# Revit family: Legrand_Digital_Management_Building_LIGHTUP_Sensor
name_source: partatom
category: Dispositifs d'éclairage
units: mm (PartAtom-declared; Revit-internal decimal feet)

## family parameters
Conserver l'orientation des annotations = Non
Cote de connecteur circulaire = Utiliser le diamètre
Couper avec des vides une fois chargée = Non
Hôte = Face
Numéro OmniClass = 23.85.80.11.27
Partagée = Non
Repere pour localisation dans la piece = Non
Titre OmniClass = Lighting Controls
Type d'élément = Normal

## types (10) — shared parameters
Bluetooth BLE = Oui
Color = White
Configurable Zones = Oui
Configurable distance = Oui
Detection angle horizontal = 360°
ETIM Class = EC001582-Movement sensor for bus system
Elévation par défaut = 2500 mm  [stored 8.2021 ft]
Fabricant = LEGRAND
Frequency = 50/60 Hz
General Conditions of Use = https://export.legrand.com
Hauteur_Saillie = 93 mm  [stored 0.305118 ft]
IK = 04
IP = 20
Installation method = Flush or surface mounting
Material = LEGRAND_PVC_BLANC
Model Product = Movement sensor
Optimum mounting height = 2500 mm  [stored 8.2021 ft]
Power supply = 240 VAC
Remote operation = Oui
Response value luminosity = 5 LUX -1275 LUX
Response value luminosity adjustable = Oui
Suitable for wireless transmission = Oui
URL = https://www.legrand.fr
With remote control = Oui
Zigbee = Oui

## per-type parameters (varying)
- CORRIDOR OCCUPANCY DETECTOR DALI: Communication Protocol=Radio 2,4 GHz;Bluetooth 5.0;DALI-2; Dali=Oui; Description=Light Up connectable presence detector for DALI broadcast circuit with variation, special for passageways; Diameter=0 mm  [stored 0 ft]; Diameter detection range on floor=0 mm  [stored 0 ft]; EAN Code=3414972281195; Etiquette_ZD_BASIC_MULTI=Non; Etiquette_ZD_CORRIDOR=Oui; Etiquette_ZD_ZS_ACTIVITY_ADVANCED=Non; Famille imbriquée=CORRIDOR_SENSOR; Height=96 mm  [stored 0.314961 ft]; Length=103 mm; Max. transmission range frontally=24000 mm  [stored 78.7402 ft]; Max. transmission range sideways=3000 mm  [stored 9.84252 ft]; Mounting height (Min-Max)=1700 mm-4000 mm; Operating temperature MIN-MAX=-10°C - +30 °C; Product designation=LIGHT UP CORRIDOR DALI DETECTOR; Reference=048554; Response value sensitivity adjustable=Oui; Sensor type=infrared; Shape detection=round; Surface detection=72 m2; Weight=213.75 g; Width=103 mm; Zones=ZD_CORRIDOR
- OCCUPANCY DETECTOR DALI: Communication Protocol=Radio 2,4 GHz;Bluetooth 5.0;DALI-2; Dali=Oui; Description=Light Up connectable presence detector for DALI broadcast circuit with variation, special workspace; Diameter=83 mm  [stored 0.27231 ft]; Diameter detection range on floor=12000 mm; EAN Code=3414972281171; Etiquette_ZD_BASIC_MULTI=Oui; Etiquette_ZD_CORRIDOR=Non; Etiquette_ZD_ZS_ACTIVITY_ADVANCED=Non; Famille imbriquée=BASIC_SENSOR; Height=83 mm  [stored 0.27231 ft]; Length=83 mm  [stored 0.27231 ft]; Max. transmission range frontally=0 mm  [stored 0 ft]; Max. transmission range sideways=0 mm  [stored 0 ft]; Mounting height (Min-Max)=1700 mm-4000 mm; Operating temperature MIN-MAX=-10°C - +30 °C; Product designation=LIGHT UP OCCUPANCY DALI DETECTOR; Reference=048552; Response value sensitivity adjustable=Oui; Sensor type=infrared; Shape detection=round; Surface detection=112 m2; Weight=142.5 g; Width=83 mm  [stored 0.27231 ft]; Zones=ZD_BASIC_MULTI
- OCCUPANCY DETECTOR ON-OFF: Communication Protocol=Radio 2,4 GHz;Bluetooth 5.0; Dali=Non; Description=Light Up ON/OFF connectable presence detector, special workspace; Diameter=83 mm  [stored 0.27231 ft]; Diameter detection range on floor=12000 mm; EAN Code=3414972281188; Etiquette_ZD_BASIC_MULTI=Oui; Etiquette_ZD_CORRIDOR=Non; Etiquette_ZD_ZS_ACTIVITY_ADVANCED=Non; Famille imbriquée=BASIC_SENSOR; Height=83 mm  [stored 0.27231 ft]; Length=83 mm  [stored 0.27231 ft]; Max. switching power=2000 W; Max. transmission range frontally=0 mm  [stored 0 ft]; Max. transmission range sideways=0 mm  [stored 0 ft]; Mounting height (Min-Max)=1700 mm-4000 mm; Operating temperature MIN-MAX=-10°C - +30 °C; Product designation=LIGHT UP OCCUPANCY ON-OFF DETECTOR; Reference=048551; Response value sensitivity adjustable=Oui; Sensor type=infrared; Shape detection=round; Surface detection=112 m2; Weight=161.5 g; Width=83 mm  [stored 0.27231 ft]; Zones=ZD_BASIC_MULTI
- OCCUPANCY DETECTOR DALI 3 ZONES: Communication Protocol=Radio 2,4 GHz;Bluetooth 5.0;DALI-2; Dali=Oui; Description=Light Up connectable presence detector for multicast DALI circuit with variation, special workspace; Diameter=83 mm  [stored 0.27231 ft]; Diameter detection range on floor=12000 mm; EAN Code=3414972406239; Etiquette_ZD_BASIC_MULTI=Oui; Etiquette_ZD_CORRIDOR=Non; Etiquette_ZD_ZS_ACTIVITY_ADVANCED=Non; Famille imbriquée=BASIC_SENSOR; Height=83 mm  [stored 0.27231 ft]; Length=83 mm  [stored 0.27231 ft]; Max. transmission range frontally=0 mm  [stored 0 ft]; Max. transmission range sideways=0 mm  [stored 0 ft]; Mounting height (Min-Max)=1700 mm-4000 mm; Operating temperature MIN-MAX=-10°C - +30 °C; Product designation=LIGHT UP OCCUPANCY DALI 3 ZONES DETECTOR; Reference=048555; Response value sensitivity adjustable=Oui; Sensor type=infrared; Shape detection=round; Surface detection=112 m2; Weight=161.5 g; Width=83 mm  [stored 0.27231 ft]; Zones=ZD_BASIC_MULTI
- CORRIDOR OCCUPANCY DETECTOR ON-OFF: Communication Protocol=Radio 2,4 GHz;Bluetooth 5.0; Dali=Non; Description=Connectable presence detector Light Up ON/OFF, special for places of passage; Diameter=103 mm; Diameter detection range on floor=0 mm  [stored 0 ft]; EAN Code=3414972281164; Etiquette_ZD_BASIC_MULTI=Non; Etiquette_ZD_CORRIDOR=Oui; Etiquette_ZD_ZS_ACTIVITY_ADVANCED=Non; Famille imbriquée=CORRIDOR_SENSOR; Height=96 mm  [stored 0.314961 ft]; Length=103 mm; Max. switching power=2000 W; Max. transmission range frontally=24000 mm  [stored 78.7402 ft]; Max. transmission range sideways=3000 mm  [stored 9.84252 ft]; Mounting height (Min-Max)=1700 mm-4000 mm; Operating temperature MIN-MAX=-10°C - +30 °C; Product designation=LIGHT UP CORRIDOR ON-OFF DETECTOR; Reference=048553; Response value sensitivity adjustable=Oui; Sensor type=infrared; Shape detection=round; Surface detection=72 m2; Weight=242.25 g; Width=103 mm; Zones=ZD_CORRIDOR
- MULTISENSOR DALI 3 ZONES DETECTOR: Communication Protocol=Radio 2,4 GHz;Bluetooth 5.0;DALI-2; Dali=Oui; Description=Light Up connectable presence detector for multicast DALI circuit with variation and environmental measurements; Diameter=103 mm; Diameter detection range on floor=12000 mm; EAN Code=3414972406253; Etiquette_ZD_BASIC_MULTI=Oui; Etiquette_ZD_CORRIDOR=Non; Etiquette_ZD_ZS_ACTIVITY_ADVANCED=Non; Famille imbriquée=MULTI_SENSOR; Height=85 mm; Length=103 mm; Max. switching power=1500 W; Max. transmission range frontally=0 mm  [stored 0 ft]; Max. transmission range sideways=0 mm  [stored 0 ft]; Mounting height (Min-Max)=1700 mm-4000 mm; Operating temperature MIN-MAX=-10°C - +30 °C; Product designation=LIGHT UP MULTISENSOR DALI 3 ZONES DETECTORv; Reference=048573; Response value sensitivity adjustable=Oui; Sensor type=infrared; Shape detection=round; Surface detection=112 m2; Weight=223.25 g; Width=103 mm; Zones=ZD_BASIC_MULTI
- MULTISENSOR DALI DETECTOR: Communication Protocol=Radio 2,4 GHz;Bluetooth 5.0;DALI-2; Dali=Oui; Description=Light Up connectable presence detector for DALI broadcast circuit with variation and environmental measurements; Diameter=103 mm; Diameter detection range on floor=12000 mm; EAN Code=3414972281157; Etiquette_ZD_BASIC_MULTI=Oui; Etiquette_ZD_CORRIDOR=Non; Etiquette_ZD_ZS_ACTIVITY_ADVANCED=Non; Famille imbriquée=MULTI_SENSOR; Height=85 mm; Length=103 mm; Max. switching power=1500 W; Max. transmission range frontally=0 mm  [stored 0 ft]; Max. transmission range sideways=0 mm  [stored 0 ft]; Mounting height (Min-Max)=1700 mm-4000 mm; Operating temperature MIN-MAX=-10°C - +30 °C; Product designation=LIGHT UP MULTISENSOR DALI DETECTOR; Reference=048571; Response value sensitivity adjustable=Oui; Sensor type=infrared; Shape detection=round; Surface detection=112 m2; Weight=223.25 g; Width=103 mm; Zones=ZD_BASIC_MULTI
- CORRIDOR OCCUPANCY DETECTOR DALI 3 ZONES: Communication Protocol=Radio 2,4 GHz;Bluetooth 5.0;DALI-2; Dali=Oui; Description=Light Up connectable presence detector for DALI multicast circuit with variation, special for passageways; Diameter=0 mm  [stored 0 ft]; Diameter detection range on floor=0 mm  [stored 0 ft]; EAN Code=3414972406246; Etiquette_ZD_BASIC_MULTI=Non; Etiquette_ZD_CORRIDOR=Oui; Etiquette_ZD_ZS_ACTIVITY_ADVANCED=Non; Famille imbriquée=CORRIDOR_SENSOR; Height=96 mm  [stored 0.314961 ft]; Length=103 mm; Max. transmission range frontally=24000 mm  [stored 78.7402 ft]; Max. transmission range sideways=3000 mm  [stored 9.84252 ft]; Mounting height (Min-Max)=1700 mm-4000 mm; Operating temperature MIN-MAX=-10°C - +30 °C; Product designation=LIGHT UP CORRIDOR DALI 3 ZONES DETECTOR; Reference=048556; Response value sensitivity adjustable=Oui; Sensor type=infrared; Shape detection=round; Surface detection=72 m2; Weight=242.25 g; Width=103 mm; Zones=ZD_CORRIDOR
- ADVANCED MULTISENSOR DALI 3 ZONES DETECTOR: Communication Protocol=Radio 2,4 GHz;Bluetooth 5.0;DALI-2; Dali=Oui; Description=Light Up connectable presence detector for multicast DALI circuit with variation, environmental measurements, people counting; Diameter=0 mm  [stored 0 ft]; Diameter detection range on floor=0 mm  [stored 0 ft]; EAN Code=3414972406260; Etiquette_ZD_BASIC_MULTI=Non; Etiquette_ZD_CORRIDOR=Non; Etiquette_ZD_ZS_ACTIVITY_ADVANCED=Oui; Famille imbriquée=ADVANCED_SENSOR; Height=77 mm; Length=157 mm; Max. switching power=1500 W; Max. transmission range frontally=8000 mm  [stored 26.2467 ft]; Max. transmission range sideways=8000 mm  [stored 26.2467 ft]; Mounting height (Min-Max)=2400 mm-4000 mm; Operating temperature MIN-MAX=5°C - +30 °C; Product designation=LIGHT UP ADVANCED MULTISENSOR DALI 3 ZONES DETECTOR; Reference=048574; Response value sensitivity adjustable=Non; Sensor type=thermal imager; Shape detection=rectangular; Surface detection=64 m2; Weight=304 g; Width=103 mm; Zones=ZD_ACTIVITY_ADVANCED
- ADVANCED MULTISENSOR DALI DETECTOR: Communication Protocol=Radio 2,4 GHz;Bluetooth 5.0;DALI-2; Dali=Oui; Description=Light Up connectable presence detector for DALI broadcast circuit with variation, environmental measurements, people counting; Diameter=0 mm  [stored 0 ft]; Diameter detection range on floor=0 mm  [stored 0 ft]; EAN Code=3414972281140; Etiquette_ZD_BASIC_MULTI=Non; Etiquette_ZD_CORRIDOR=Non; Etiquette_ZD_ZS_ACTIVITY_ADVANCED=Oui; Famille imbriquée=ADVANCED_SENSOR; Height=77 mm; Length=157 mm; Max. switching power=1500 W; Max. transmission range frontally=8000 mm  [stored 26.2467 ft]; Max. transmission range sideways=8000 mm  [stored 26.2467 ft]; Mounting height (Min-Max)=2400 mm-4000 mm; Operating temperature MIN-MAX=5°C - +30 °C; Product designation=LIGHT UP ADVANCED MULTISENSOR DALI DETECTOR; Reference=048572; Response value sensitivity adjustable=Non; Sensor type=thermal imager; Shape detection=rectangular; Surface detection=64 m2; Weight=304 g; Width=103 mm; Zones=ZD_ACTIVITY_ADVANCED

note: [stored X ft] marks values corroborated as IEEE doubles in the binary element streams (Revit-internal decimal feet)
